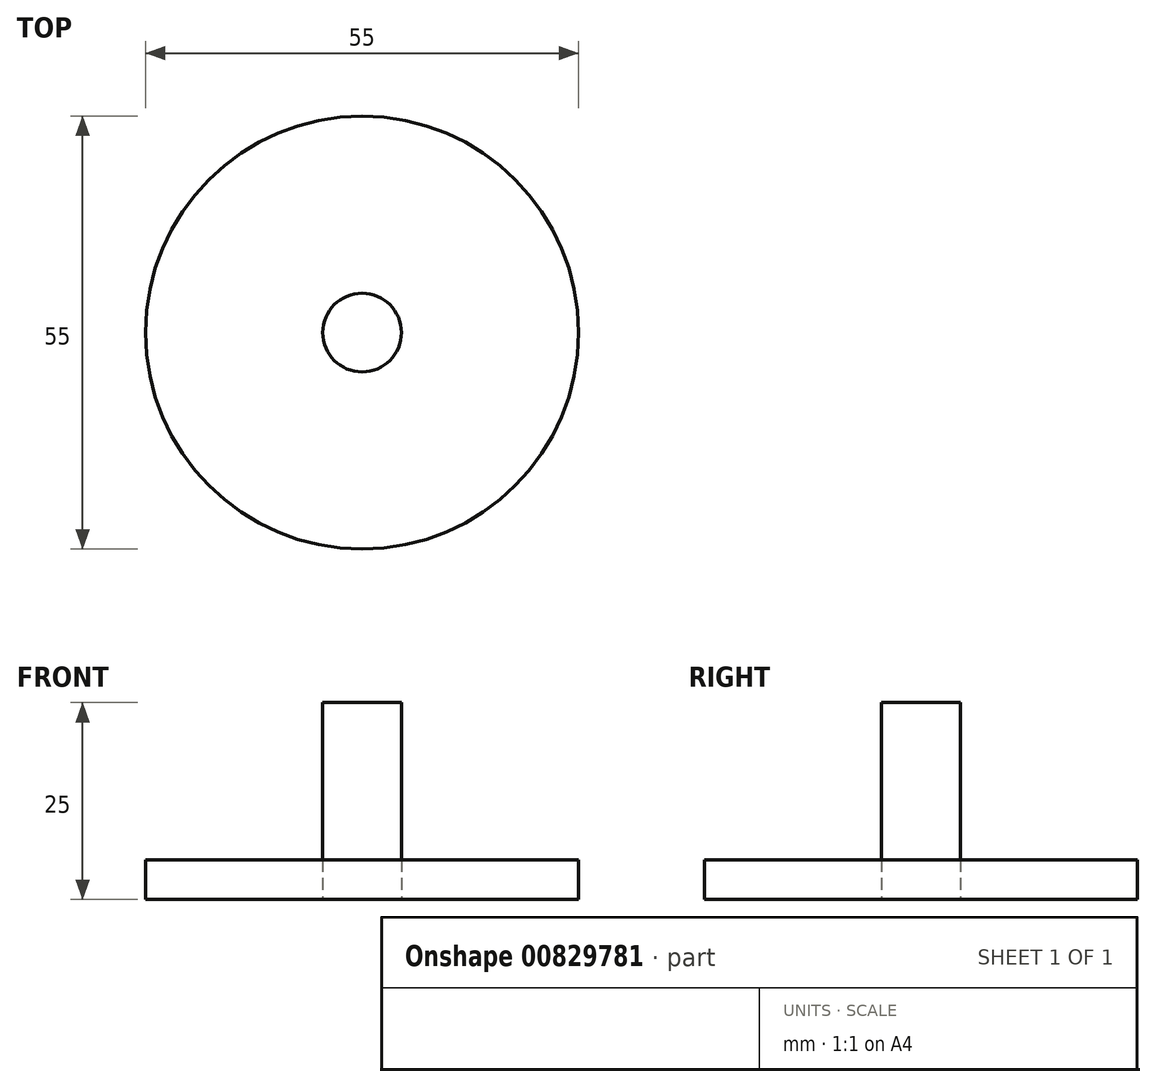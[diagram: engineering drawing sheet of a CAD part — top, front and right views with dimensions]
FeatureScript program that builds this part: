
annotation { "Feature Type Name" : "Feature", "Feature Type Description" : "" }
export const myFeature = defineFeature(function(context is Context, id is Id, definition is map)
    precondition{}
    {
        {
            var Q0;
            Q0=qCreatedBy(makeId("Top.planeOp"),FACE);
            var sketch = newSketch(context, id + "F0", { "sketchPlane" : qUnion([Q0])});
            skCircle(sketch, "E0", {"center": v(0, 0) * mm, "radius": 27.5 * mm});
            skCircle(sketch, "E1", {"center": v(0, 0) * mm, "radius": 12.5 * mm});
            skPoint(sketch, "E2", {"position": v(-25, 0) * mm});
            skPoint(sketch, "E3", {"position": v(-20, 0) * mm});
            skPoint(sketch, "E4", {"position": v(-15, 0) * mm});
            skLineSegment(sketch, "E5", {"start": v(0, 0) * mm, "end": v(-27.5, 0) * mm});
            skSolve(sketch);
        }
        {
            var Q0;
            Q0=qCreatedBy(makeId("Front.planeOp"),FACE);
            var sketch = newSketch(context, id + "F1", { "sketchPlane" : qUnion([Q0])});
            skPoint(sketch, "E6", {"position": v(-25, 0) * mm});
            skPoint(sketch, "E7", {"position": v(-20, 0) * mm});
            skPoint(sketch, "E8", {"position": v(-15, 0) * mm});
            skLineSegment(sketch, "E9", {"start": v(-15, 0) * mm, "end": v(-15, -10) * mm});
            skLineSegment(sketch, "E10", {"start": v(-20, 0) * mm, "end": v(-20, -10) * mm});
            skLineSegment(sketch, "E11", {"start": v(-25, 0) * mm, "end": v(-25, -10) * mm});
            skLineSegment(sketch, "E12", {"start": v(-25, -10) * mm, "end": v(-26, -10) * mm});
            skLineSegment(sketch, "E13", {"start": v(-20, -10) * mm, "end": v(-21, -10) * mm});
            skLineSegment(sketch, "E14", {"start": v(-15, -10) * mm, "end": v(-16, -10) * mm});
            skLineSegment(sketch, "E15", {"start": v(-25, -10) * mm, "end": v(-25, -12) * mm});
            skLineSegment(sketch, "E16", {"start": v(-25, -12) * mm, "end": v(-26, -10) * mm});
            skLineSegment(sketch, "E17", {"start": v(-20, -10) * mm, "end": v(-20, -12) * mm});
            skLineSegment(sketch, "E18", {"start": v(-20, -12) * mm, "end": v(-21, -10) * mm});
            skLineSegment(sketch, "E19", {"start": v(-15, -10) * mm, "end": v(-15, -12) * mm});
            skLineSegment(sketch, "E20", {"start": v(-15, -12) * mm, "end": v(-16, -10) * mm});
            skLineSegment(sketch, "E21", {"start": v(-26, -10) * mm, "end": v(-26, 0) * mm});
            skLineSegment(sketch, "E22", {"start": v(-21, -10) * mm, "end": v(-21, 0) * mm});
            skLineSegment(sketch, "E23", {"start": v(-16, -10) * mm, "end": v(-16, 0) * mm});
            skLineSegment(sketch, "E24", {"start": v(-25, 0) * mm, "end": v(-26, 0) * mm});
            skLineSegment(sketch, "E25", {"start": v(-20, 0) * mm, "end": v(-21, 0) * mm});
            skLineSegment(sketch, "E26", {"start": v(-15, 0) * mm, "end": v(-16, 0) * mm});
            skLineSegment(sketch, "E27", {"start": v(0, 0) * mm, "end": v(0, 25) * mm});
            skLineSegment(sketch, "E28", {"start": v(0, 25) * mm, "end": v(-5, 25) * mm});
            skLineSegment(sketch, "E29", {"start": v(-5, 25) * mm, "end": v(-5, 0) * mm});
            skLineSegment(sketch, "E30", {"start": v(-5, 0) * mm, "end": v(0, 0) * mm});
            skSolve(sketch);
        }
        {
            var Q0;
            Q0=sQuery(id+"F1.wireOp",EDGE,"E24");
            var Q1;
            Q1=sQuery(id+"F1.wireOp",EDGE,"E21");
            var Q2;
            Q2=sQuery(id+"F1.wireOp",EDGE,"E16");
            var Q3;
            Q3=sQuery(id+"F1.wireOp",EDGE,"E11");
            revolve(context, id + "F2", {"bodyType" : ToolBodyType.SURFACE, "surfaceOperationType" : NewSurfaceOperationType.NEW, "surfaceEntities" : qUnion([Q0, Q1, Q2]), "axis" : qUnion([Q3]), "revolveType" : RevolveType.FULL});
        }
        {
            var Q0;
            Q0=sQuery(id+"F1.wireOp",EDGE,"E22");
            var Q1;
            Q1=sQuery(id+"F1.wireOp",EDGE,"E25");
            var Q2;
            Q2=sQuery(id+"F1.wireOp",EDGE,"E18");
            var Q3;
            Q3=sQuery(id+"F1.wireOp",EDGE,"E10");
            revolve(context, id + "F3", {"bodyType" : ToolBodyType.SURFACE, "surfaceOperationType" : NewSurfaceOperationType.NEW, "surfaceEntities" : qUnion([Q0, Q1, Q2]), "axis" : qUnion([Q3]), "revolveType" : RevolveType.FULL});
        }
        {
            var Q0;
            Q0=sQuery(id+"F1.wireOp",EDGE,"E23");
            var Q1;
            Q1=sQuery(id+"F1.wireOp",EDGE,"E26");
            var Q2;
            Q2=sQuery(id+"F1.wireOp",EDGE,"E20");
            var Q3;
            Q3=sQuery(id+"F1.wireOp",EDGE,"E9");
            revolve(context, id + "F4", {"bodyType" : ToolBodyType.SURFACE, "surfaceOperationType" : NewSurfaceOperationType.NEW, "surfaceEntities" : qUnion([Q0, Q1, Q2]), "axis" : qUnion([Q3]), "revolveType" : RevolveType.FULL});
        }
        {
            var Q0;
            Q0=qCreatedBy(makeId("Front.planeOp"),FACE);
            var sketch = newSketch(context, id + "F5", { "sketchPlane" : qUnion([Q0])});
            skLineSegment(sketch, "E31", {"start": v(0, 23.81) * mm, "end": v(0, -24.67) * mm});
            skSolve(sketch);
        }
        {
            var Q0;
            Q0=makeQuery(id+"F2.opRevolve","SWEPT_BODY",BODY,{"disambiguationData":[OSD([sQuery(id+"F1.wireOp",EDGE,"E16")])]});
            var Q1;
            Q1=sQuery(id+"F5.wireOp",EDGE,"E31");
            circularPattern(context, id + "F6", {"entities" : qUnion([Q0]), "axis" : qUnion([Q1]), "angle" : 360 * degree, "instanceCount" : 24, "equalSpace" : true});
        }
        {
            var Q0;
            Q0=makeQuery(id+"F3.opRevolve","SWEPT_BODY",BODY,{"disambiguationData":[OSD([sQuery(id+"F1.wireOp",EDGE,"E18")])]});
            var Q1;
            Q1=sQuery(id+"F5.wireOp",EDGE,"E31");
            circularPattern(context, id + "F7", {"entities" : qUnion([Q0]), "axis" : qUnion([Q1]), "angle" : 360 * degree, "instanceCount" : 18, "equalSpace" : true});
        }
        {
            var Q0;
            Q0=makeQuery(id+"F4.opRevolve","SWEPT_BODY",BODY,{"disambiguationData":[OSD([sQuery(id+"F1.wireOp",EDGE,"E20")])]});
            var Q1;
            Q1=sQuery(id+"F5.wireOp",EDGE,"E31");
            circularPattern(context, id + "F8", {"entities" : qUnion([Q0]), "axis" : qUnion([Q1]), "angle" : 360 * degree, "instanceCount" : 12, "equalSpace" : true});
        }
        {
            var Q0;
            Q0=sQuery(id+"F0.wireOp",EDGE,"E5");
            var Q1;
            Q1=sQuery(id+"F5.wireOp",EDGE,"E31");
            revolve(context, id + "F9", {"bodyType" : ToolBodyType.SURFACE, "surfaceOperationType" : NewSurfaceOperationType.NEW, "surfaceEntities" : qUnion([Q0]), "axis" : qUnion([Q1]), "revolveType" : RevolveType.FULL});
        }
        {
            var Q0;
            Q0=makeQuery(id+"F9.opRevolve","SWEPT_FACE",FACE,{"disambiguationData":[OSD([sQuery(id+"F0.wireOp",EDGE,"E5")])]});
            extrude(context, id + "F10", {"entities" : qUnion([Q0]), "depth" : -5 * mm, "offsetDistance" : 25 * mm});
        }
        {
            var Q0;
            Q0=makeQuery(id+"F1.imprint","IMPRINT",FACE,{"disambiguationData":[TD([[makeQuery(id+"F1.imprint","IMPRINT",EDGE,{"derivedFrom":sQuery(id+"F1.wireOp",EDGE,"E27")}),1.0]])]});
            var Q1;
            Q1=sQuery(id+"F1.wireOp",EDGE,"E27");
            revolve(context, id + "F11", {"surfaceOperationType" : NewSurfaceOperationType.NEW, "entities" : qUnion([Q0]), "axis" : qUnion([Q1]), "revolveType" : RevolveType.FULL});
        }
    });
